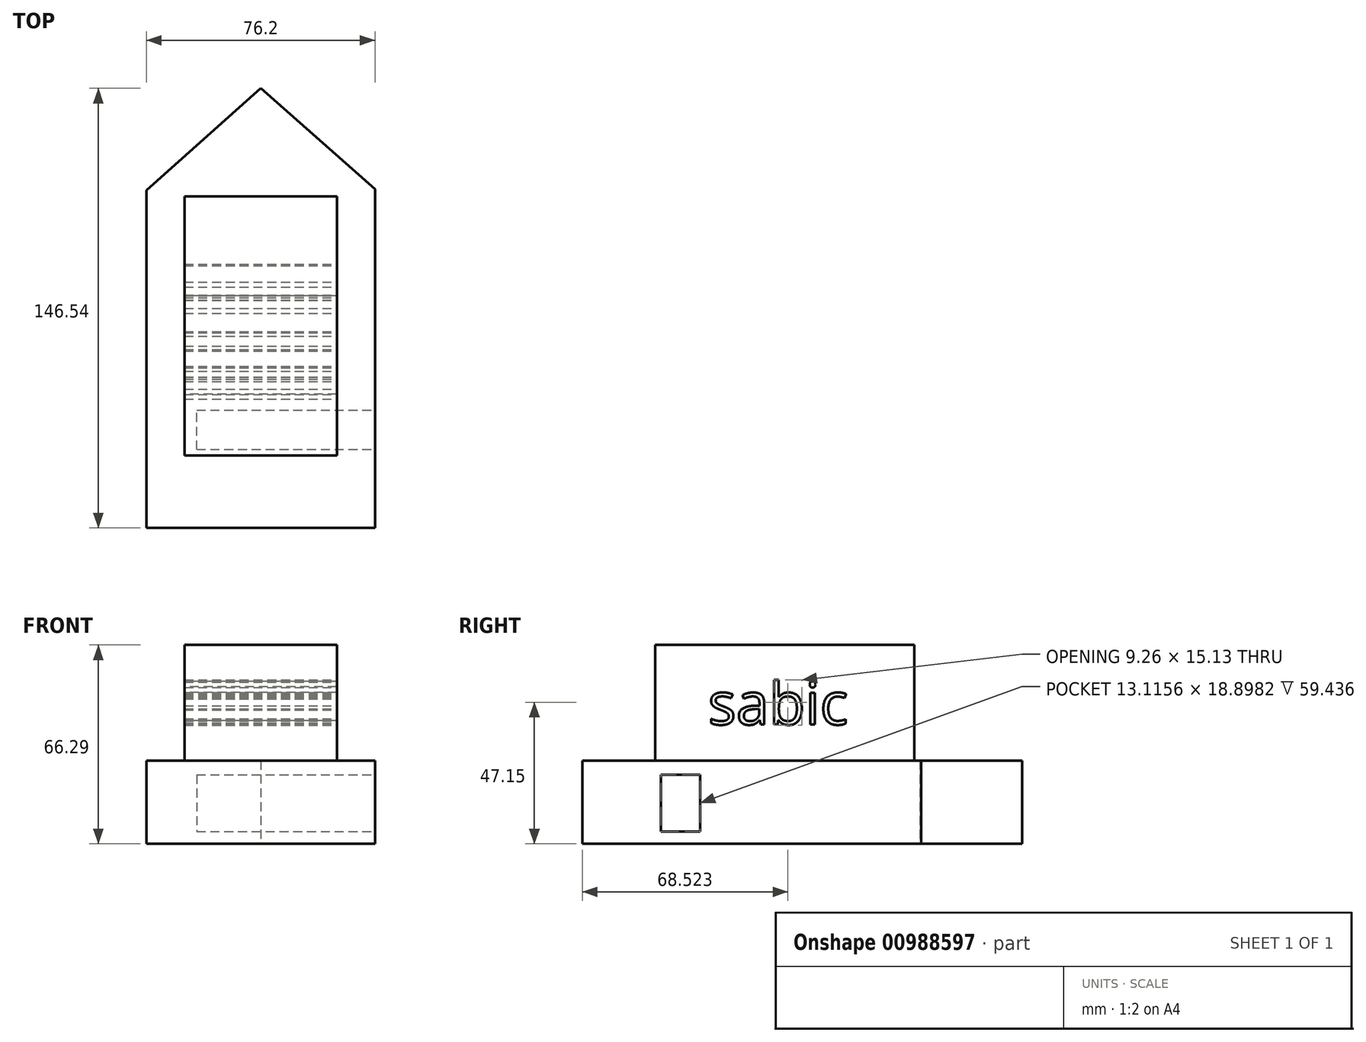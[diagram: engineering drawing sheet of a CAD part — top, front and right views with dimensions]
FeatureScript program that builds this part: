
annotation { "Feature Type Name" : "Feature", "Feature Type Description" : "" }
export const myFeature = defineFeature(function(context is Context, id is Id, definition is map)
    precondition{}
    {
        {
            var Q0;
            Q0=qCreatedBy(makeId("Top.planeOp"),FACE);
            var sketch = newSketch(context, id + "F0", { "sketchPlane" : qUnion([Q0])});
            skLineSegment(sketch, "E0", {"start": v(0, 74.05) * mm, "end": v(-38.1, 40.05) * mm});
            skLineSegment(sketch, "E1", {"start": v(-38.1, 40.05) * mm, "end": v(-38.1, -72.49) * mm});
            skLineSegment(sketch, "E2", {"start": v(-38.1, -72.49) * mm, "end": v(38.1, -72.49) * mm});
            skLineSegment(sketch, "E3", {"start": v(38.1, -72.49) * mm, "end": v(38.1, 40.44) * mm});
            skLineSegment(sketch, "E4", {"start": v(38.1, 40.44) * mm, "end": v(0, 74.05) * mm});
            skSolve(sketch);
        }
        {
            var Q0;
            Q0=qCreatedBy(makeId("Top.planeOp"),FACE);
            var sketch = newSketch(context, id + "F1", { "sketchPlane" : qUnion([Q0])});
            skLineSegment(sketch, "E5.bottom", {"start": v(25.4, 38.1) * mm, "end": v(-25.4, 38.1) * mm});
            skLineSegment(sketch, "E5.top", {"start": v(25.4, -48.26) * mm, "end": v(-25.4, -48.26) * mm});
            skLineSegment(sketch, "E5.left", {"start": v(25.4, 38.1) * mm, "end": v(25.4, -48.26) * mm});
            skLineSegment(sketch, "E5.right", {"start": v(-25.4, 38.1) * mm, "end": v(-25.4, -48.26) * mm});
            skSolve(sketch);
        }
        {
            var Q0;
            Q0 = qSketchRegion(id + "F0", true);
            extrude(context, id + "F2", {"entities" : qUnion([Q0]), "depth" : 27.7 * mm, "offsetDistance" : 25.4 * mm});
        }
        {
            var Q0;
            Q0=makeQuery(id+"F1.imprint","IMPRINT",FACE,{"disambiguationData":[TD([[makeQuery(id+"F1.imprint","IMPRINT",EDGE,{"derivedFrom":sQuery(id+"F1.wireOp",EDGE,"E5.bottom")}),1.0]])]});
            extrude(context, id + "F3", {"entities" : qUnion([Q0]), "operationType" : NewBodyOperationType.ADD, "depth" : 66.3 * mm, "offsetDistance" : 25.4 * mm});
        }
        {
            var Q0;
            Q0=makeQuery(id+"F3.opExtrude","CAP_FACE",FACE,{"disambiguationData":[OSD([sQuery(id+"F1.wireOp",EDGE,"E5.bottom"),sQuery(id+"F1.wireOp",EDGE,"E5.top"),sQuery(id+"F1.wireOp",EDGE,"E5.left"),sQuery(id+"F1.wireOp",EDGE,"E5.right")])],"isStart":false});
            var sketch = newSketch(context, id + "F4", { "sketchPlane" : qUnion([Q0])});
            skCircle(sketch, "E6", {"center": v(0, 24.4) * mm, "radius": 6.35 * mm});
            skCircle(sketch, "E7", {"center": v(0, -1) * mm, "radius": 6.35 * mm});
            skCircle(sketch, "E8", {"center": v(0, -26.4) * mm, "radius": 6.35 * mm});
            skSolve(sketch);
        }
        {
            var Q0;
            Q0=sQuery(id+"F4.wireOp",EDGE,"E7");
            var Q1;
            Q1=sQuery(id+"F4.wireOp",EDGE,"E8");
            var Q2;
            Q2=sQuery(id+"F4.wireOp",EDGE,"E6");
            extrude(context, id + "F5", {"bodyType" : ToolBodyType.SURFACE, "surfaceEntities" : qUnion([Q0, Q1, Q2]), "depth" : 54.1 * mm, "offsetDistance" : 25.4 * mm});
        }
        {
            var Q0;
            Q0=makeQuery(id+"F3.opExtrude","SWEPT_FACE",FACE,{"disambiguationData":[OSD([sQuery(id+"F1.wireOp",EDGE,"E5.left")])]});
            var sketch = newSketch(context, id + "F6", { "sketchPlane" : qUnion([Q0])});
            skText(sketch, "E9", { "text": "sabic", "fontName": "OpenSans-Regular.ttf"});
            const initialGuessF6  = {"E9": [-0.03059, 0.03978, 1, 0, 0.01415]};
            skSetInitialGuess(sketch, initialGuessF6);
            skSolve(sketch);
        }
        {
            var Q0;
            Q0 = qSketchRegion(id + "F6", true);
            extrude(context, id + "F7", {"entities" : qUnion([Q0]), "operationType" : NewBodyOperationType.REMOVE, "oppositeDirection" : true, "depth" : 195.33 * mm, "offsetDistance" : 25.4 * mm});
        }
        {
            var Q0;
            Q0=makeQuery(id+"F2.opExtrude","SWEPT_FACE",FACE,{"disambiguationData":[OSD([sQuery(id+"F0.wireOp",EDGE,"E3")])]});
            var sketch = newSketch(context, id + "F8", { "sketchPlane" : qUnion([Q0])});
            skLineSegment(sketch, "E10.bottom", {"start": v(-46.34, 23.03) * mm, "end": v(-33.22, 23.03) * mm});
            skLineSegment(sketch, "E10.top", {"start": v(-46.34, 4.13) * mm, "end": v(-33.22, 4.13) * mm});
            skLineSegment(sketch, "E10.left", {"start": v(-46.34, 23.03) * mm, "end": v(-46.34, 4.13) * mm});
            skLineSegment(sketch, "E10.right", {"start": v(-33.22, 23.03) * mm, "end": v(-33.22, 4.13) * mm});
            skSolve(sketch);
        }
        {
            var Q0;
            Q0 = qSketchRegion(id + "F8", true);
            extrude(context, id + "F9", {"entities" : qUnion([Q0]), "operationType" : NewBodyOperationType.REMOVE, "oppositeDirection" : true, "depth" : 59.44 * mm, "offsetDistance" : 25.4 * mm});
        }
    });
